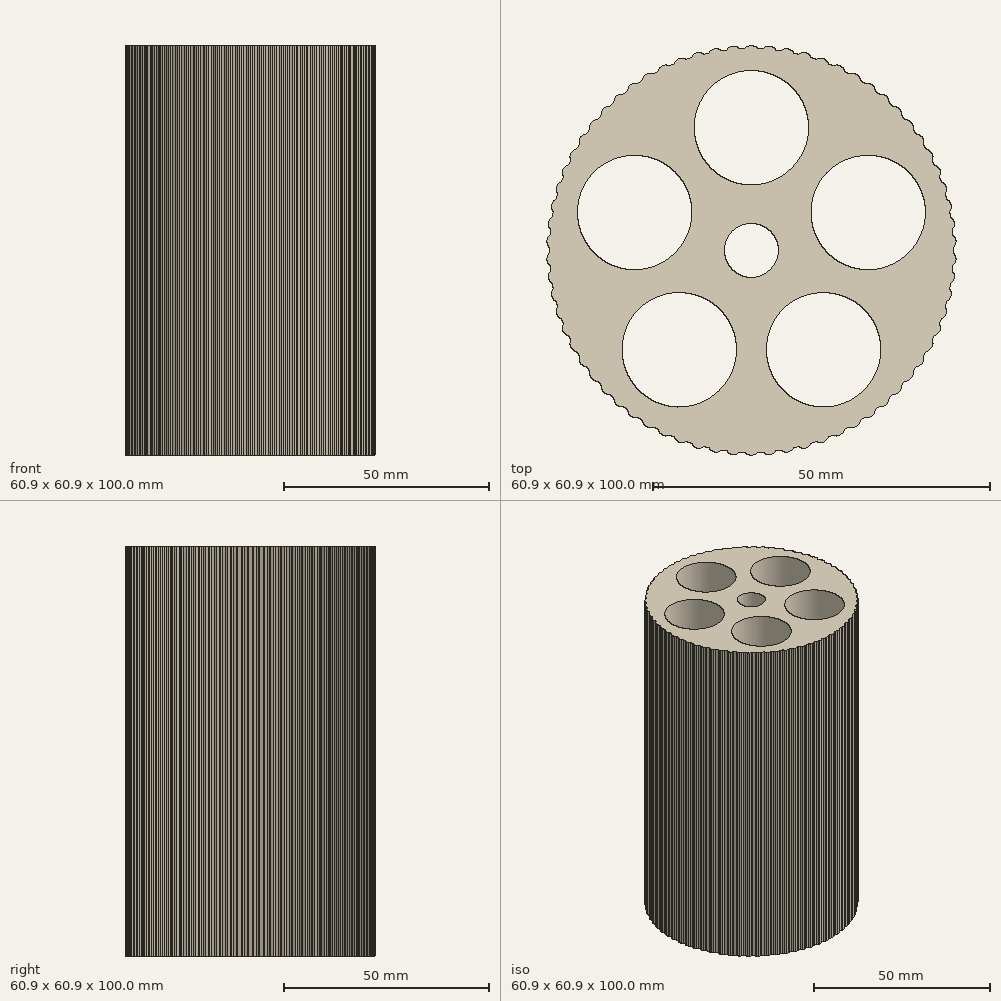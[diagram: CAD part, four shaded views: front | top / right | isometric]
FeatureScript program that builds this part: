
annotation { "Feature Type Name" : "Feature", "Feature Type Description" : "" }
export const myFeature = defineFeature(function(context is Context, id is Id, definition is map)
    precondition{}
    {
        {
            var Q0;
            Q0=qCreatedBy(makeId("Top.planeOp"),FACE);
            var sketch = newSketch(context, id + "F0", { "sketchPlane" : qUnion([Q0])});
            skCircle(sketch, "E0", {"center": v(0, 0) * mm, "radius": 30 * mm});
            skCircle(sketch, "E1", {"center": v(0, 0) * mm, "radius": 4 * mm});
            skCircle(sketch, "E2", {"center": v(0, 18.24) * mm, "radius": 8.5 * mm});
            skCircle(sketch, "E3.1.0", {"center": v(-17.35, 5.64) * mm, "radius": 8.5 * mm});
            skCircle(sketch, "E3.2.0", {"center": v(-10.72, -14.76) * mm, "radius": 8.5 * mm});
            skCircle(sketch, "E3.3.0", {"center": v(10.72, -14.76) * mm, "radius": 8.5 * mm});
            skCircle(sketch, "E3.4.0", {"center": v(17.35, 5.64) * mm, "radius": 8.5 * mm});
            skSolve(sketch);
        }
        {
            var Q0;
            Q0=makeQuery(id+"F0.imprint","IMPRINT",FACE,{"disambiguationData":[TD([[makeQuery(id+"F0.imprint","IMPRINT",EDGE,{"derivedFrom":sQuery(id+"F0.wireOp",EDGE,"E0")}),1.0]])]});
            extrude(context, id + "F1", {"entities" : qUnion([Q0]), "depth" : 100 * mm, "offsetDistance" : 25 * mm});
        }
        {
            var Q0;
            Q0=qCreatedBy(makeId("Top.planeOp"),FACE);
            var sketch = newSketch(context, id + "F2", { "sketchPlane" : qUnion([Q0])});
            skLineSegment(sketch, "E4.MirrorCS", {"start": v(0, 30.46) * mm, "end": v(0.56, 30.34) * mm});
            skLineSegment(sketch, "E5", {"start": v(0.56, 30.34) * mm, "end": v(1.14, 29.84) * mm});
            skLineSegment(sketch, "E6", {"start": v(1.14, 29.84) * mm, "end": v(0, 29.84) * mm});
            skLineSegment(sketch, "E7.MirrorCS", {"start": v(0, 30.46) * mm, "end": v(-0.56, 30.34) * mm});
            skLineSegment(sketch, "E8.MirrorCS", {"start": v(-0.56, 30.34) * mm, "end": v(-1.14, 29.84) * mm});
            skLineSegment(sketch, "E9.MirrorCS", {"start": v(-1.14, 29.84) * mm, "end": v(0, 29.84) * mm});
            skSolve(sketch);
        }
        {
            var Q0;
            Q0=makeQuery(id+"F2.imprint","IMPRINT",FACE,{"disambiguationData":[TD([[makeQuery(id+"F2.imprint","IMPRINT",EDGE,{"derivedFrom":sQuery(id+"F2.wireOp",EDGE,"E4.MirrorCS")}),-1.0]])]});
            extrude(context, id + "F3", {"entities" : qUnion([Q0]), "depth" : 100 * mm, "offsetDistance" : 25 * mm});
        }
        {
            var Q0;
            Q0=makeQuery(id+"F3.opExtrude","SWEPT_BODY",BODY,{"disambiguationData":[OSD([sQuery(id+"F2.wireOp",EDGE,"E4.MirrorCS"),sQuery(id+"F2.wireOp",EDGE,"E5"),sQuery(id+"F2.wireOp",EDGE,"E6"),sQuery(id+"F2.wireOp",EDGE,"E7.MirrorCS"),sQuery(id+"F2.wireOp",EDGE,"E8.MirrorCS"),sQuery(id+"F2.wireOp",EDGE,"E9.MirrorCS")])]});
            var Q1;
            Q1=makeQuery(id+"F1.opExtrude","SWEPT_FACE",FACE,{"disambiguationData":[OSD([sQuery(id+"F0.wireOp",EDGE,"E1")])]});
            circularPattern(context, id + "F4", {"operationType" : NewBodyOperationType.ADD, "entities" : qUnion([Q0]), "axis" : qUnion([Q1]), "angle" : 360 * degree, "instanceCount" : 70, "oppositeDirection" : true, "equalSpace" : true});
        }
    });
